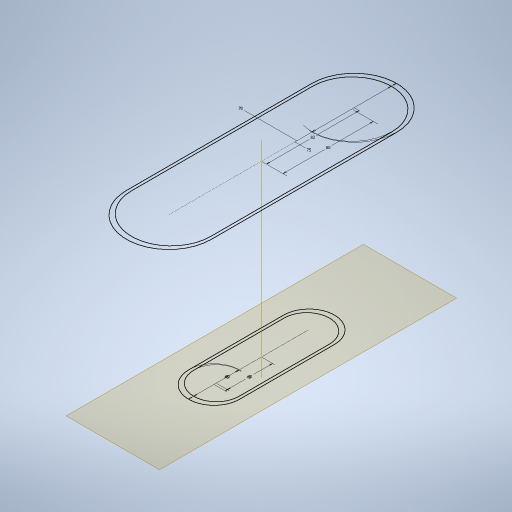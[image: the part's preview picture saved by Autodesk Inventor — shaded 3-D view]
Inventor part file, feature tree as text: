
AUTODESK INVENTOR PART (.ipt)
format: ipt  version: 2023 (Build 270158000, 158)  size: 270,848 bytes
history: native  units: mm
features: sketch x4, plane x1
ambient origin geometry x8: Origin, YZ Plane, XZ Plane, XY Plane, X Axis, Y Axis, Z Axis, Center Point
feature tree (5):
  sketch  "Sketch1"  dims[d0=80.0mm]
  sketch  "Sketch2"  dims[d1=70.0mm]
  plane  "Work Plane2"
  sketch  "Sketch3"  dims[d2=82.0mm]
  sketch  "Sketch4"  dims[d3=75.0mm d4=-150.0mm d5=40.0mm d6=40.0mm d7=42.0mm d8=45.0mm]
